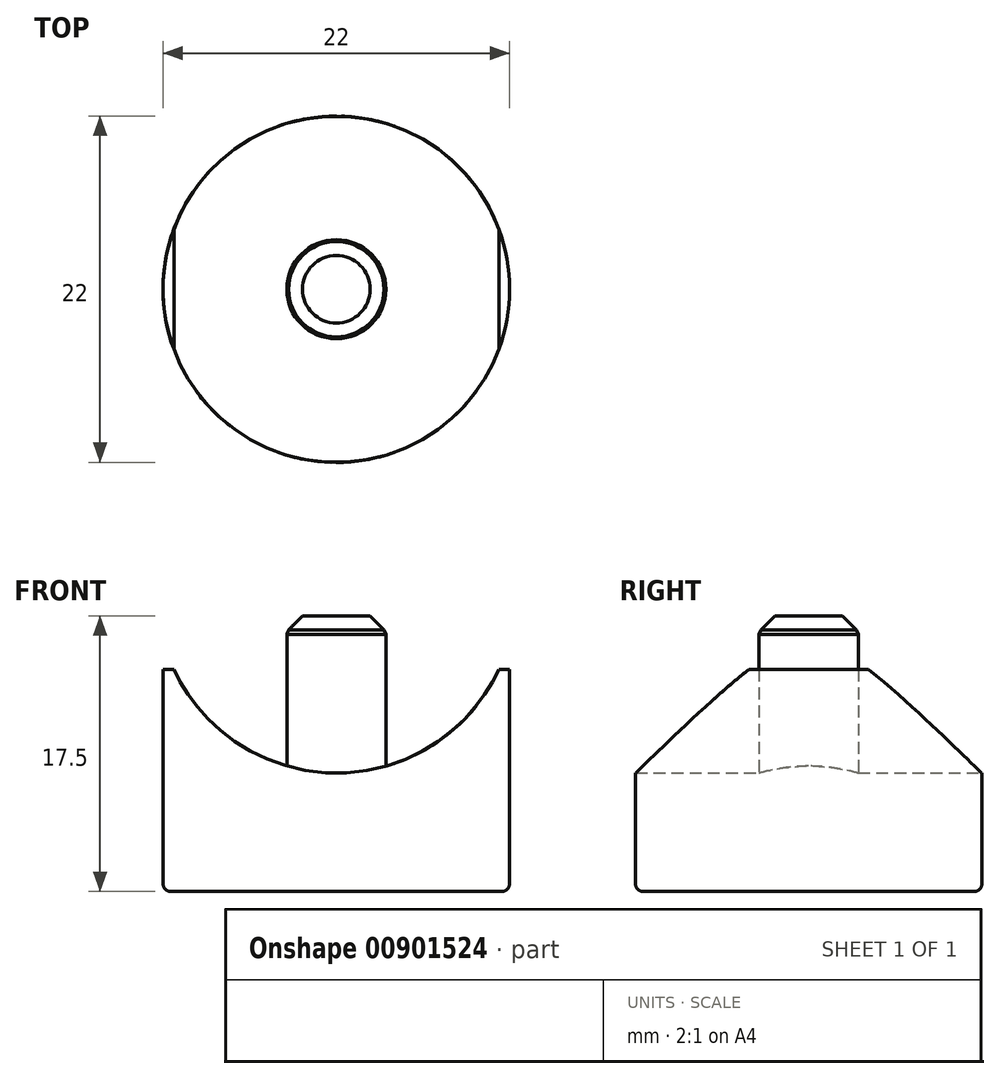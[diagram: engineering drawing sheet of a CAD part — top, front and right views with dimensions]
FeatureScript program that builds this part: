
annotation { "Feature Type Name" : "Feature", "Feature Type Description" : "" }
export const myFeature = defineFeature(function(context is Context, id is Id, definition is map)
    precondition{}
    {
        {
            var Q0;
            Q0=qCreatedBy(makeId("Top.planeOp"),FACE);
            var sketch = newSketch(context, id + "F0", { "sketchPlane" : qUnion([Q0])});
            skCircle(sketch, "E0", {"center": v(0, -12.36) * mm, "radius": 11 * mm});
            skSolve(sketch);
        }
        {
            var Q0;
            Q0=makeQuery(id+"F0.imprint","IMPRINT",FACE,{"disambiguationData":[TD([[makeQuery(id+"F0.imprint","IMPRINT",EDGE,{"derivedFrom":sQuery(id+"F0.wireOp",EDGE,"E0")}),1.0]])]});
            extrude(context, id + "F1", {"entities" : qUnion([Q0]), "depth" : 14.1 * mm, "offsetDistance" : 25 * mm});
        }
        {
            var Q0;
            Q0=qCreatedBy(makeId("Front.planeOp"),FACE);
            var sketch = newSketch(context, id + "F2", { "sketchPlane" : qUnion([Q0])});
            skCircle(sketch, "E1", {"center": v(0, 18.9) * mm, "radius": 11.38 * mm});
            skSolve(sketch);
        }
        {
            var Q0;
            Q0 = qSketchRegion(id + "F2", true);
            extrude(context, id + "F3", {"entities" : qUnion([Q0]), "operationType" : NewBodyOperationType.REMOVE, "depth" : 28.4 * mm, "offsetDistance" : 25 * mm});
        }
        {
            var Q0;
            Q0=makeQuery(id+"F1.opExtrude","CAP_FACE",FACE,{"disambiguationData":[OSD([sQuery(id+"F0.wireOp",EDGE,"E0")])],"isStart":true});
            var sketch = newSketch(context, id + "F4", { "sketchPlane" : qUnion([Q0])});
            skLineSegment(sketch, "E2", {"start": v(0, 1.36) * mm, "end": v(0, 23.36) * mm});
            skCircle(sketch, "E3", {"center": v(0, 12.36) * mm, "radius": 3.15 * mm});
            skSolve(sketch);
        }
        {
            var Q0;
            Q0 = qSketchRegion(id + "F4", true);
            extrude(context, id + "F5", {"entities" : qUnion([Q0]), "operationType" : NewBodyOperationType.ADD, "oppositeDirection" : true, "depth" : 17.5 * mm, "offsetDistance" : 25 * mm});
        }
        {
            var Q0;
            Q0=makeQuery(id+"F5.opExtrude","CAP_EDGE",EDGE,{"disambiguationData":[OSD([sQuery(id+"F4.wireOp",EDGE,"E3")])],"isStart":false});
            chamfer(context, id + "F6", {"entities" : qUnion([Q0]), "width" : 1 * mm, "tangentPropagation" : true});
        }
        {
            var Q0;
            Q0=makeQuery(id+"F1.opExtrude","CAP_EDGE",EDGE,{"disambiguationData":[OSD([sQuery(id+"F0.wireOp",EDGE,"E0")])],"isStart":true});
            fillet(context, id + "F7", {"entities" : qUnion([Q0]), "radius" : 0.48 * mm, "tangentPropagation" : true, "allowEdgeOverflow" : false});
        }
        {
            var Q0;
            {var subQ0=sQuery(id+"F4.wireOp",EDGE,"E3");Q0=makeQuery(id+"F6.opChamfer","BLEND_EDGE",EDGE,{"blendedFrom":[makeQuery(id+"F5.opExtrude","CAP_EDGE",EDGE,{"disambiguationData":[OSD([subQ0])],"isStart":false}),makeQuery(id+"F5.opExtrude","SWEPT_FACE",FACE,{"disambiguationData":[OSD([subQ0])]})],"blendedInto":[makeQuery(id+"F5.opExtrude","SWEPT_FACE",FACE,{"disambiguationData":[OSD([subQ0])]})]});}
            chamfer(context, id + "F8", {"entities" : qUnion([Q0]), "width" : 0.4 * mm, "tangentPropagation" : true});
        }
    });
